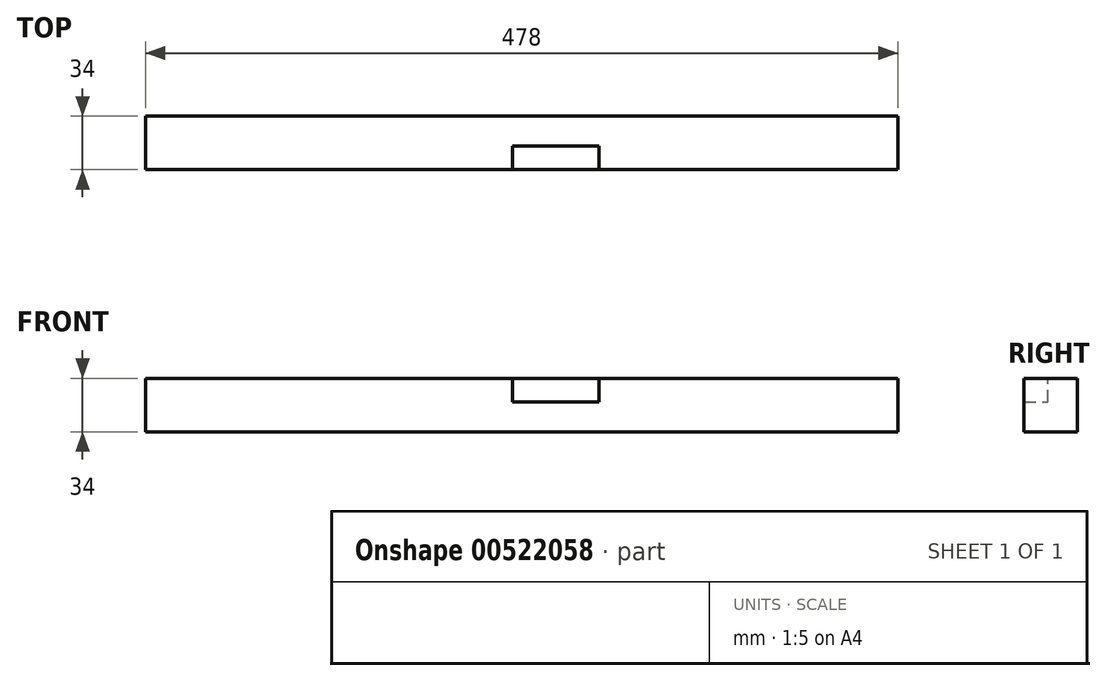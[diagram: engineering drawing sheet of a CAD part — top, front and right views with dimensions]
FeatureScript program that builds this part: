
annotation { "Feature Type Name" : "Feature", "Feature Type Description" : "" }
export const myFeature = defineFeature(function(context is Context, id is Id, definition is map)
    precondition{}
    {
        {
            var Q0;
            Q0=qCreatedBy(makeId("Right.planeOp"),FACE);
            var sketch = newSketch(context, id + "F0", { "sketchPlane" : qUnion([Q0])});
            skLineSegment(sketch, "E0.bottom", {"start": v(0, 0) * mm, "end": v(-34, 0) * mm});
            skLineSegment(sketch, "E0.top", {"start": v(0, 34) * mm, "end": v(-34, 34) * mm});
            skLineSegment(sketch, "E0.left", {"start": v(0, 0) * mm, "end": v(0, 34) * mm});
            skLineSegment(sketch, "E0.right", {"start": v(-34, 0) * mm, "end": v(-34, 34) * mm});
            skSolve(sketch);
        }
        {
            var Q0;
            Q0=makeQuery(id+"F0.imprint","IMPRINT",FACE,{"disambiguationData":[TD([[makeQuery(id+"F0.imprint","IMPRINT",EDGE,{"derivedFrom":sQuery(id+"F0.wireOp",EDGE,"E0.bottom")}),-1.0]])]});
            extrude(context, id + "F1", {"entities" : qUnion([Q0]), "oppositeDirection" : true, "depth" : 478 * mm, "offsetDistance" : 25 * mm});
        }
        {
            var Q0;
            Q0=makeQuery(id+"F1.opExtrude","SWEPT_FACE",FACE,{"disambiguationData":[OSD([sQuery(id+"F0.wireOp",EDGE,"E0.top")])]});
            var sketch = newSketch(context, id + "F2", { "sketchPlane" : qUnion([Q0])});
            skLineSegment(sketch, "E1.bottom", {"start": v(-190, -34) * mm, "end": v(-245, -34) * mm});
            skLineSegment(sketch, "E1.top", {"start": v(-190, -19) * mm, "end": v(-245, -19) * mm});
            skLineSegment(sketch, "E1.left", {"start": v(-190, -34) * mm, "end": v(-190, -19) * mm});
            skLineSegment(sketch, "E1.right", {"start": v(-245, -34) * mm, "end": v(-245, -19) * mm});
            skSolve(sketch);
        }
        {
            var Q0;
            Q0=makeQuery(id+"F2.imprint","IMPRINT",FACE,{"disambiguationData":[TD([[makeQuery(id+"F2.imprint","IMPRINT",EDGE,{"derivedFrom":sQuery(id+"F2.wireOp",EDGE,"E1.bottom")}),1.0]])]});
            extrude(context, id + "F3", {"entities" : qUnion([Q0]), "operationType" : NewBodyOperationType.REMOVE, "oppositeDirection" : true, "depth" : 15 * mm, "offsetDistance" : 25 * mm});
        }
    });
